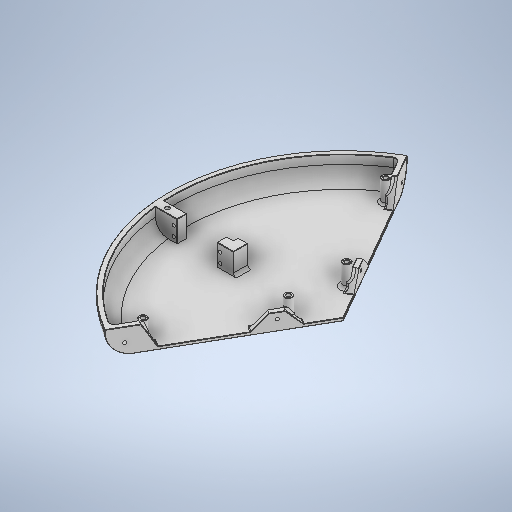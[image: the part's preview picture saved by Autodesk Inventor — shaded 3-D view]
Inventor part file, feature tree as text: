
AUTODESK INVENTOR PART (.ipt)
format: ipt  version: 2025.1 (Build 291241000, 241)  size: 944,128 bytes
history: native  units: mm
features: extrude x12, sketch x12, fillet x11, chamfer x4
ambient origin geometry x8: Origin, YZ Plane, XZ Plane, XY Plane, X Axis, Y Axis, Z Axis, Center Point
bodies: Solid1 (feature_tree)
feature tree (39):
  extrude  "Extrusion1"  TaperAngle=60.0deg  [1 undecoded]
  extrude  "Extrusion2"  Depth=22.0mm TaperAngle=0.0deg
  extrude  "Extrusion4"  Depth=3.3mm
  extrude  "Extrusion5"  Depth=15.0mm TaperAngle=0.0deg
  extrude  "Extrusion8"  Depth=3.3mm
  extrude  "Extrusion9"  Depth=15.0mm TaperAngle=0.0deg
  extrude  "Extrusion10"  Depth=9.8mm
  fillet  "Rundung2"  Radius=55.0mm
  fillet  "Rundung3"  Radius=41.0mm
  fillet  "Rundung5"  Radius=110.5mm
  extrude  "Extrusion13"  Depth=3.0mm
  extrude  "Extrusion14"  TaperAngle=0.0deg  [1 undecoded]
  fillet  "Rundung6"  Radius=10.0mm
  extrude  "Extrusion15"  Depth=350.0mm
  extrude  "Extrusion11"  Depth=10.0mm
  extrude  "Extrusion12"  Depth=10.0mm
  chamfer  "Fasen1"  Distance=22.0mm
  fillet  "Rundung10"  Radius=13.0mm
  fillet  "Rundung11"  Radius=22.0mm
  fillet  "Rundung13"  Radius=3.0mm
  fillet  "Rundung14"  Radius=8.0mm
  fillet  "Rundung15"  Radius=8.0mm
  fillet  "Rundung16"  Radius=3.0mm
  fillet  "Rundung17"  Radius=30.0mm
  chamfer  "Fasen2"  Distance=8.0mm
  chamfer  "Fasen3"  Distance=8.0mm
  chamfer  "Fasen4"  Distance=30.0mm
  sketch  "Sketch1"  dims[d3=180.0mm d4=60.0deg]
  sketch  "Sketch4"  dims[d5=120.0deg d7=22.0mm d8=0.0mm]
  sketch  "Sketch8"  dims[d47=0.0mm d48=0.0mm d68=3.3mm]
  sketch  "Sketch9"  dims[d70=50.0mm d72=15.0mm d73=0.0mm]
  sketch  "Sketch12"  dims[d74=3.3mm d75=3.3mm]
  sketch  "Skizze13"  dims[d76=50.0mm d78=15.0mm d79=0.0mm]
  sketch  "Skizze15"  dims[d93=3.0mm d94=0.0mm d98=9.8mm d99=55.0mm d101=41.0mm d102=110.5mm]
  sketch  "Skizze16"  dims[d104=41.0mm d105=3.0mm]
  sketch  "Skizze17"  dims[d109=-2.0mm d110=0.0mm d111=10.0mm]
  sketch  "Skizze19"  dims[d112=22.0mm d113=0.0mm d115=350.0mm]
  sketch  "Skizze22"  dims[d116=120.0deg d117=10.0mm]
  sketch  "Skizze23"  dims[d118=10.0mm d119=10.0mm d120=22.0mm d121=0.0mm d122=13.0mm d123=22.0mm d127=3.0mm d128=8.0mm d129=8.0mm d130=3.0mm d132=30.0mm d133=8.0mm d134=8.0mm d136=30.0mm d137=3.0mm d138=3.0mm d139=22.0mm d140=0.0mm d141=4.1mm d142=8.0mm d143=0.0mm d145=3.0mm d146=10.0mm d147=10.0mm d148=3.3mm d149=3.3mm d150=3.3mm d151=3.3mm d153=3.4mm d154=3.4mm d155=3.4mm d156=3.4mm d157=4.8mm d158=4.8mm d159=5.0mm d160=0.0mm d161=115.0mm d164=115.0mm d165=60.0deg d169=0.0mm d171=5.0mm d172=0.0mm d173=4.0mm d175=8.0mm d176=8.0mm d177=8.0mm d178=8.0mm d179=60.0deg d180=45.0deg d182=5.0mm d183=0.0mm d185=0.0mm d188=45.0deg d193=25.0mm d194=20.0mm d195=20.0mm d196=45.0deg d197=6.0mm d198=20.0mm d199=45.0deg d200=20.0mm d201=25.0mm d202=6.0mm d207=0.4mm d208=2.0mm d209=45.0deg d210=125.0mm d211=125.0mm d212=5.0mm d213=5.0mm d214=3.0mm d215=2.0mm d217=0.0mm d218=180.0deg d219=2.0mm d220=2.0mm d221=4.0mm d222=2.0mm d223=2.0mm d224=5.0mm d225=4.1mm d226=15.0mm d227=0.4mm d228=2.0mm d229=45.0deg d230=0.4mm d231=2.0mm d232=45.0deg d233=0.4mm d234=2.0mm d235=45.0deg d54=1.0mm d55=1.0mm d56=1.0mm d57=0.15mm d58=0.25mm d59=0.375mm d60=14.3117mm d61=0.75mm d62=20.594885mm d63=0.0625mm d64=0.75mm d65=0.375mm d85=0.5mm d86=0.872665mm d87=0.5mm d88=0.872665mm d96=0.5mm d97=0.872665mm]
note: 2 required parameter values undecoded (feature->parameter linkage not recoverable at this tier; creation-order binding heuristic only, values carry confidence <= 0.55)
